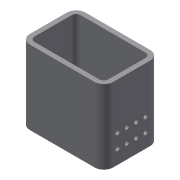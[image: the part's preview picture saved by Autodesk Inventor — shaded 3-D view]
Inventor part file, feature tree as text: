
AUTODESK INVENTOR PART (.ipt)
format: ipt  version: 2016 (Build 200138000, 138)  size: 160,256 bytes
history: native  units: in
note: dims shown in document units (in); Inventor stores cm internally (conversion verified against a paired STEP export)
features: extrude x3, sketch x3
ambient origin geometry x8: Origin, YZ Plane, XZ Plane, XY Plane, X Axis, Y Axis, Z Axis, Center Point
bodies: Solid1 (feature_tree)
feature tree (6):
  extrude  "Extrusion1"  Depth=24.0in
  extrude  "Extrusion3"  Depth=4.0in
  extrude  "Extrusion4"  Depth=30.0in TaperAngle=0.0deg
  sketch  "Sketch1"  dims[d0=36.0in d1=24.0in]
  sketch  "Sketch3"  dims[d2=2.0in d3=0.0in d9=4.0in]
  sketch  "Sketch10"  dims[d10=2.0in d11=30.0in d12=0.0in d56=1.7717in d57=1.7717in d58=1.7717in d59=1.7717in d60=2.0in d61=4.0in d62=4.0in d63=4.0in d64=6.0in d65=1.0in d66=0.0in d67=1.7717in d68=1.7717in d69=1.7717in d70=1.7717in d71=6.0in]
